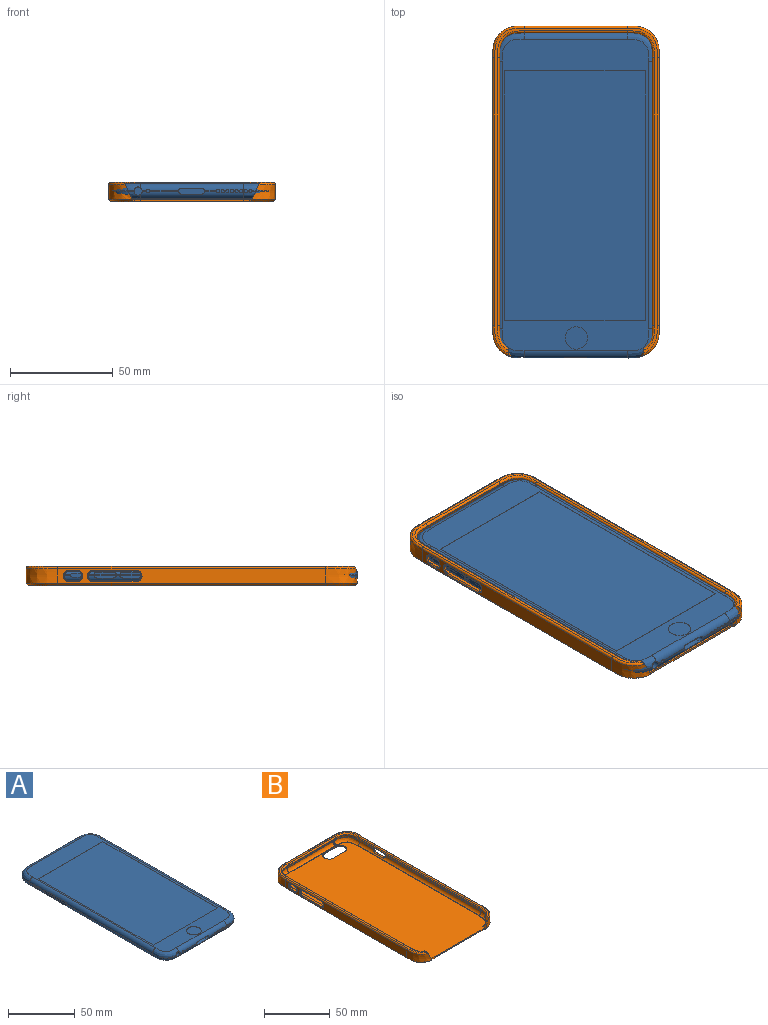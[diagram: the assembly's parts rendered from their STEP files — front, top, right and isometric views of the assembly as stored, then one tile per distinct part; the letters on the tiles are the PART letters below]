
ASSEMBLY  parts=2 mates=1
PART A: 108 faces, bbox 79.2x158.7x8 mm
  f0: plane 4.66x0.2mm, normal (-1,0,0), area 0.9mm2, adj f20,f43,f51,f102
  f1: plane 1.68x0.2mm, normal (-1,0,0), area 0.3mm2, adj f43,f51,f90,f95
  f2: plane 5.7x0.2mm, normal (-1,0,0), area 1.1mm2, adj f43,f51,f88,f104
  f3: plane 103.64x0.2mm, normal (1,0,0), area 20.7mm2, adj f12,f42,f50,f81
  f4: plane 0.66x0.2mm, normal (0,-1,0), area 0.1mm2, adj f46,f54,f72,f74
  f5: plane 0.2x0.15mm, normal (0,-1,0), area 0mm2, adj f16,f46,f54,f72
  f6: plane 5.71x0.2mm, normal (0,-1,0), area 1.1mm2, adj f46,f54,f59,f70
  f7: plane 0.66x0.2mm, normal (0,-1,0), area 0.1mm2, adj f46,f54,f65,f74
  f8: plane 0.66x0.2mm, normal (0,-1,0), area 0.1mm2, adj f46,f54,f63,f65
  f9: plane 0.66x0.2mm, normal (0,-1,0), area 0.1mm2, adj f46,f54,f61,f63
  f10: plane 0.66x0.2mm, normal (0,-1,0), area 0.1mm2, adj f46,f54,f59,f61
  f11: plane 14.01x0.2mm, normal (0,-1,0), area 2.8mm2, adj f46,f54,f57,f68
  f12: extruded ~13.98x9.78mm, area 3.8mm2, adj f3,f44,f52,f78
  f13: extruded ~0.66x0.2mm, area 0.1mm2, adj f44,f52,f76,f78
  f14: plane 151.62x71.34mm, normal (0,0,1), area 2367.4mm2, adj f30,f32,f33,f34,f35,f47,f48,f49
  f15: plane 2.09x0.2mm, normal (0,-1,0), area 0.4mm2, adj f46,f54,f55,f57
  f16: extruded ~0.52x0.2mm, area 0.1mm2, adj f5,f44,f52,f76
  f17: plane 15.88x0.2mm, normal (1,0,0), area 3.2mm2, adj f18,f42,f50,f83
  f18: extruded ~14.13x14.13mm, area 4.7mm2, adj f17,f19,f38,f40,f48
  f19: plane 50.18x0.2mm, normal (0,1,0), area 10mm2, adj f18,f20,f37,f39,f47
  f20: extruded ~14.13x14.13mm, area 4.7mm2, adj f0,f19,f41,f49
  f21: plane 90.97x0.2mm, normal (-1,0,0), area 18.2mm2, adj f22,f43,f51,f97
  f22: extruded ~14.08x11.12mm, area 4.1mm2, adj f21,f45,f53,f55
  f23: plane 151.62x71.34mm, normal (0,0,-1), area 10708mm2, adj f24,f26,f28,f39,f40,f41,f42,f43
  f24: cylinder r=3.83mm len=7.66mm, axis (0,0,1), area 16.1mm2, adj f23,f25,f37,f38
  f25: plane 7.66x7.66mm, normal (0,0,-1), area 46.1mm2, adj f24
  f26: cylinder r=0.8mm len=1.6mm, axis (0,0,-1), area 0.5mm2, adj f23,f27
  f27: plane 1.6x1.6mm, normal (0,0,-1), area 2mm2, adj f26
  f28: cylinder r=2.06mm len=4.11mm, axis (0,0,-1), area 1.3mm2, adj f23,f29
  f29: plane 4.11x4.11mm, normal (0,0,-1), area 13.3mm2, adj f28
  f30: cylinder r=5.45mm len=10.9mm, axis (0,0,1), area 3.4mm2, adj f14,f31
  f31: plane 10.9x10.9mm, normal (0,0,1), area 93.3mm2, adj f30
  f32: plane 68.36x0.1mm, normal (0,-1,0), area 6.8mm2, adj f14,f33,f35,f36
  f33: plane 121.54x0.1mm, normal (1,0,0), area 12.2mm2, adj f14,f32,f34,f36
  f34: plane 68.36x0.1mm, normal (0,1,0), area 6.8mm2, adj f14,f33,f35,f36
  f35: plane 121.54x0.1mm, normal (-1,0,0), area 12.2mm2, adj f14,f32,f34,f36
  f36: plane 121.54x68.36mm, normal (0,0,1), area 8308.5mm2, adj f32,f33,f34,f35
  f37: bspline ~3.66x3.64mm, area 4.8mm2, adj f19,f24,f38,f39
  f38: bspline ~3.61x3.6mm, area 5.3mm2, adj f18,f24,f37,f40
  f39: cylinder r=3.55mm len=49.3mm, axis (-1,0,0), area 274.9mm2, adj f19,f23,f37,f41
  f40: bspline ~16.8x14.8mm, area 114.8mm2, adj f18,f23,f38,f42
  f41: bspline ~16.8x16.8mm, area 120.2mm2, adj f20,f23,f39,f43
  f42: cylinder r=3.55mm len=130.46mm, axis (0,1,0), area 727.5mm2, adj f3,f17,f23,f40,f44,f80
  f43: cylinder r=3.55mm len=130.46mm, axis (0,-1,0), area 727.5mm2, adj f0,f1,f2,f21,f23,f41,f45,f87
  f44: bspline ~16.8x16.8mm, area 118.5mm2, adj f12,f13,f16,f23,f42,f46,f76,f78
  f45: bspline ~16.8x16.8mm, area 117.7mm2, adj f22,f23,f43,f46,f55
  f46: cylinder r=3.55mm len=50.18mm, axis (1,0,0), area 255.6mm2, adj f4,f5,f6,f7,f8,f9,f10,f11
  f47: cylinder r=3.55mm len=50.18mm, axis (1,0,0), area 279.8mm2, adj f14,f19,f48,f49
  f48: bspline ~16.8x16.8mm, area 120.2mm2, adj f14,f18,f47,f50
  f49: bspline ~16.8x14.8mm, area 120.2mm2, adj f14,f20,f47,f51
  f50: cylinder r=3.55mm len=130.46mm, axis (0,-1,0), area 727.5mm2, adj f3,f14,f17,f48,f52,f86
  f51: cylinder r=3.55mm len=130.46mm, axis (0,1,0), area 727.5mm2, adj f0,f1,f2,f14,f21,f49,f53,f93
  f52: bspline ~16.8x16.8mm, area 118.4mm2, adj f12,f13,f14,f16,f50,f54,f76,f78
  f53: bspline ~16.8x16.8mm, area 117.7mm2, adj f14,f22,f51,f54,f55
  f54: cylinder r=3.55mm len=50.18mm, axis (-1,0,0), area 255.6mm2, adj f4,f5,f6,f7,f8,f9,f10,f11
  f55: cylinder r=2.01mm len=4.02mm, axis (0,-1,0), area 34.2mm2, adj f15,f22,f45,f46,f53,f54,f56
  f56: plane 4.02x4.02mm, normal (0,-1,0), area 12.7mm2, adj f55
  f57: cylinder r=0.8mm len=3mm, axis (0,-1,0), area 14.9mm2, adj f11,f15,f46,f54,f58
  f58: plane 1.6x1.6mm, normal (0,-1,0), area 2mm2, adj f57
  f59: cylinder r=0.8mm len=3mm, axis (0,-1,0), area 14.9mm2, adj f6,f10,f46,f54,f60
  f60: plane 1.6x1.6mm, normal (0,-1,0), area 2mm2, adj f59
  f61: cylinder r=0.8mm len=3mm, axis (0,-1,0), area 14.9mm2, adj f9,f10,f46,f54,f62
  f62: plane 1.6x1.6mm, normal (0,-1,0), area 2mm2, adj f61
  f63: cylinder r=0.8mm len=3mm, axis (0,-1,0), area 14.9mm2, adj f8,f9,f46,f54,f64
  f64: plane 1.6x1.6mm, normal (0,-1,0), area 2mm2, adj f63
  f65: cylinder r=0.8mm len=3mm, axis (0,-1,0), area 14.9mm2, adj f7,f8,f46,f54,f66
  f66: plane 1.6x1.6mm, normal (0,-1,0), area 2mm2, adj f65
  f67: plane 9.84x2.72mm, normal (0,0,-1), area 26.8mm2, adj f54,f68,f70,f71
  f68: cylinder r=1.47mm len=3mm, axis (0,-1,0), area 13.3mm2, adj f11,f46,f54,f67,f69,f71
  f69: plane 9.84x2.72mm, normal (0,0,1), area 26.8mm2, adj f46,f68,f70,f71
  f70: cylinder r=1.47mm len=3mm, axis (0,-1,0), area 13.3mm2, adj f6,f46,f54,f67,f69,f71
  f71: plane 12.79x2.95mm, normal (0,-1,0), area 35.9mm2, adj f67,f68,f69,f70
  f72: cylinder r=0.8mm len=3mm, axis (0,-1,0), area 15.1mm2, adj f4,f5,f46,f54,f73
  f73: plane 1.6x1.6mm, normal (0,-1,0), area 2mm2, adj f72
  f74: cylinder r=0.8mm len=3mm, axis (0,-1,0), area 15.1mm2, adj f4,f7,f46,f54,f75
  f75: plane 1.6x1.6mm, normal (0,-1,0), area 2mm2, adj f74
  f76: cylinder r=0.8mm len=3mm, axis (0,-1,0), area 14.9mm2, adj f13,f16,f44,f52,f77
  f77: plane 1.6x1.6mm, normal (0,-1,0), area 2mm2, adj f76
  f78: cylinder r=0.8mm len=2.96mm, axis (0,-1,0), area 14.6mm2, adj f12,f13,f44,f52,f79
  f79: plane 1.6x1.6mm, normal (0,-1,0), area 2mm2, adj f78
  f80: plane 10.93x1.3mm, normal (-1,0,0), area 13.4mm2, adj f42,f81,f82,f83
  f81: cylinder r=1.4mm len=2.8mm, axis (-1,0,0), area 1.3mm2, adj f3,f80,f82,f84,f85,f86
  f82: plane 8.14x0.3mm, normal (0,0,-1), area 2.4mm2, adj f80,f81,f83,f85
  f83: cylinder r=1.4mm len=2.8mm, axis (-1,0,0), area 1.3mm2, adj f17,f80,f82,f84,f85,f86
  f84: plane 8.14x0.3mm, normal (0,0,1), area 2.4mm2, adj f81,f83,f85,f86
  f85: plane 10.94x2.8mm, normal (1,0,0), area 28.9mm2, adj f81,f82,f83,f84
  f86: plane 10.93x1.3mm, normal (-1,0,0), area 13.4mm2, adj f50,f81,f83,f84
  f87: plane 10.94x1.32mm, normal (1,0,0), area 13.6mm2, adj f43,f88,f89,f90
  f88: cylinder r=1.4mm len=2.8mm, axis (1,0,0), area 1.3mm2, adj f2,f87,f89,f91,f92,f93
  f89: plane 8.14x0.3mm, normal (0,0,-1), area 2.4mm2, adj f87,f88,f90,f92
  f90: cylinder r=1.4mm len=2.8mm, axis (1,0,0), area 1.3mm2, adj f1,f87,f89,f91,f92,f93
  f91: plane 8.14x0.3mm, normal (0,0,1), area 2.4mm2, adj f88,f90,f92,f93
  f92: plane 10.94x2.8mm, normal (-1,0,0), area 28.9mm2, adj f88,f89,f90,f91
  f93: plane 10.93x1.28mm, normal (1,0,0), area 13.2mm2, adj f51,f88,f90,f91
  f94: plane 10.94x1.32mm, normal (1,0,0), area 13.6mm2, adj f43,f95,f96,f97
  f95: cylinder r=1.4mm len=2.8mm, axis (1,0,0), area 1.3mm2, adj f1,f94,f96,f98,f99,f100
  f96: plane 8.14x0.3mm, normal (0,0,-1), area 2.4mm2, adj f94,f95,f97,f99
  f97: cylinder r=1.4mm len=2.8mm, axis (1,0,0), area 1.3mm2, adj f21,f94,f96,f98,f99,f100
  f98: plane 8.14x0.3mm, normal (0,0,1), area 2.4mm2, adj f95,f97,f99,f100
  f99: plane 10.94x2.8mm, normal (-1,0,0), area 28.9mm2, adj f95,f96,f97,f98
  f100: plane 10.93x1.28mm, normal (1,0,0), area 13.2mm2, adj f51,f95,f97,f98
  f101: plane 5.6x0.89mm, normal (1,0,0), area 4.6mm2, adj f43,f102,f103,f104
  f102: cylinder r=0.98mm len=1.97mm, axis (1,0,0), area 1.3mm2, adj f0,f101,f103,f105,f106,f107
  f103: plane 3.64x0.43mm, normal (0,0,-1), area 1.6mm2, adj f101,f102,f104,f106
  f104: cylinder r=0.98mm len=1.97mm, axis (1,0,0), area 1.3mm2, adj f2,f101,f103,f105,f106,f107
  f105: plane 3.64x0.43mm, normal (0,0,1), area 1.6mm2, adj f102,f104,f106,f107
  f106: plane 5.61x1.97mm, normal (-1,0,0), area 10.2mm2, adj f102,f103,f104,f105
  f107: plane 5.6x0.88mm, normal (1,0,0), area 4.5mm2, adj f51,f102,f104,f105
PART B: 108 faces, bbox 81.6x161.8x9.7 mm
  f0: extruded ~15.39x11.51mm, area 145.7mm2, adj f23,f66,f82,f89
  f1: plane 159.64x79.46mm, normal (0,0,-1), area 12304.5mm2, adj f26,f27,f28,f29,f68,f69,f70,f71
  f2: extruded ~12.01x8.14mm, area 5.8mm2, adj f6,f10,f30,f67
  f3: extruded ~11.19x4.91mm, area 4.6mm2, adj f7,f16,f67,f81
  f4: extruded ~15.39x11.51mm, area 145.7mm2, adj f17,f67,f85,f95
  f5: extruded ~13.79x8.49mm, area 3.6mm2, adj f6,f7,f39,f67
  f6: bspline ~16.7x10.56mm, area 69.8mm2, adj f2,f5,f50,f67
  f7: bspline ~16.52x9.41mm, area 62.5mm2, adj f3,f5,f53,f67
  f8: plane 50.22x0.4mm, normal (0,-1,0), area 17.9mm2, adj f9,f11,f30,f46,f47,f48
  f9: extruded ~12.13x12.13mm, area 7.3mm2, adj f8,f10,f30,f34,f47
  f10: plane 130.46x0.36mm, normal (-1,0,0), area 46.5mm2, adj f2,f9,f30,f50
  f11: extruded ~12.13x12.13mm, area 7.3mm2, adj f8,f13,f30,f49
  f12: extruded ~12.01x8.14mm, area 5.8mm2, adj f13,f30,f36,f66
  f13: plane 130.46x0.36mm, normal (1,0,0), area 46.5mm2, adj f11,f12,f30,f35
  f14: plane 50.18x0.36mm, normal (0,-1,0), area 17.9mm2, adj f15,f20,f51,f78
  f15: extruded ~12.13x12.13mm, area 7.3mm2, adj f14,f16,f31,f79
  f16: plane 130.46x0.36mm, normal (-1,0,0), area 46.5mm2, adj f3,f15,f53,f80
  f17: plane 130.46x7.3mm, normal (1,0,0), area 878.7mm2, adj f4,f18,f87,f94,f104,f105,f106,f107
  f18: extruded ~15.57x15.5mm, area 189mm2, adj f17,f24,f88,f93
  f19: plane 158.46x79.18mm, normal (0,0,1), area 530.1mm2, adj f66,f67,f75,f76,f77,f78,f79,f80
  f20: extruded ~12.13x12.13mm, area 7.3mm2, adj f14,f22,f52,f77
  f21: extruded ~11.19x4.91mm, area 4.6mm2, adj f22,f32,f66,f75
  f22: plane 130.46x0.36mm, normal (1,0,0), area 46.5mm2, adj f20,f21,f33,f76
  f23: plane 130.46x7.3mm, normal (-1,0,0), area 758.1mm2, adj f0,f25,f83,f90,f96,f97,f98,f99
  f24: plane 50.19x7.31mm, normal (0,1,0), area 366.3mm2, adj f18,f25,f86,f92
  f25: extruded ~15.57x15.5mm, area 189mm2, adj f23,f24,f84,f91
  f26: cylinder r=4.85mm len=9.71mm, axis (0,0,1), area 15.3mm2, adj f1,f27,f29,f30
  f27: plane 12.06x1mm, normal (0,1,0), area 12.1mm2, adj f1,f26,f28,f30
  f28: cylinder r=4.85mm len=9.71mm, axis (0,0,1), area 15.3mm2, adj f1,f27,f29,f30
  f29: plane 12.06x1mm, normal (0,-1,0), area 12.1mm2, adj f1,f26,f28,f30
  f30: plane 157.67x74.44mm, normal (0,0,1), area 11374mm2, adj f2,f8,f9,f10,f11,f12,f13,f26
  f31: bspline ~16.8x16.8mm, area 89.3mm2, adj f15,f41,f51,f53
  f32: bspline ~16.53x9.44mm, area 62.5mm2, adj f21,f33,f45,f66
  f33: cylinder r=3.55mm len=130.46mm, axis (0,1,0), area 445.8mm2, adj f22,f32,f37,f38,f44,f52,f54,f56
  f34: bspline ~16.8x14.8mm, area 85.5mm2, adj f9,f41,f47,f50
  f35: cylinder r=3.55mm len=130.46mm, axis (0,-1,0), area 444.5mm2, adj f13,f36,f37,f38,f44,f49,f55,f56
  f36: bspline ~16.69x10.51mm, area 69.8mm2, adj f12,f35,f45,f66
  f37: plane 3.24x0.2mm, normal (1,0,0), area 0.6mm2, adj f33,f35,f43,f60
  f38: plane 3.28x0.2mm, normal (1,0,0), area 0.7mm2, adj f33,f35,f56,f61
  f39: plane 102.64x0.2mm, normal (-1,0,0), area 20.5mm2, adj f5,f50,f53,f63
  f40: plane 14.88x0.2mm, normal (-1,0,0), area 3mm2, adj f41,f50,f53,f65
  f41: extruded ~14.13x14.13mm, area 4.7mm2, adj f31,f34,f40,f42,f47
  f42: plane 50.18x0.2mm, normal (0,-1,0), area 10mm2, adj f41,f43,f46,f48,f51
  f43: extruded ~14.13x14.13mm, area 4.7mm2, adj f37,f42,f49,f52
  f44: plane 89.96x0.2mm, normal (1,0,0), area 18mm2, adj f33,f35,f45,f57
  f45: extruded ~13.79x8.49mm, area 3.6mm2, adj f32,f36,f44,f66
  f46: bspline ~3.66x3.64mm, area 3.5mm2, adj f8,f42,f47,f48
  f47: bspline ~3.61x3.6mm, area 3.8mm2, adj f8,f9,f34,f41,f46
  f48: cylinder r=3.55mm len=49.3mm, axis (-1,0,0), area 195.8mm2, adj f8,f42,f46,f49
  f49: bspline ~16.8x16.8mm, area 89.3mm2, adj f11,f35,f43,f48
  f50: cylinder r=3.55mm len=130.46mm, axis (0,1,0), area 491.9mm2, adj f6,f10,f34,f39,f40,f62,f63,f65
  f51: cylinder r=3.55mm len=50.18mm, axis (1,0,0), area 199.3mm2, adj f14,f31,f42,f52
  f52: bspline ~16.8x14.8mm, area 89.3mm2, adj f20,f33,f43,f51
  f53: cylinder r=3.55mm len=130.46mm, axis (0,-1,0), area 491.9mm2, adj f7,f16,f31,f39,f40,f63,f64,f65
  f54: plane 20.75x1.7mm, normal (0,0,-1), area 35.2mm2, adj f33,f56,f57,f96
  f55: plane 20.75x1.73mm, normal (0,0,1), area 35.9mm2, adj f35,f56,f57,f99
  f56: cylinder r=2.4mm len=4.8mm, axis (-1,0,0), area 9.6mm2, adj f33,f35,f38,f54,f55,f97
  f57: cylinder r=2.4mm len=4.8mm, axis (-1,0,0), area 9.6mm2, adj f33,f35,f44,f54,f55,f98
  f58: plane 3.64x1.71mm, normal (0,0,-1), area 6.2mm2, adj f33,f60,f61,f100
  f59: plane 3.64x1.72mm, normal (0,0,1), area 6.3mm2, adj f35,f60,f61,f103
  f60: cylinder r=2.4mm len=4.8mm, axis (-1,0,0), area 9.6mm2, adj f33,f35,f37,f58,f59,f101
  f61: cylinder r=2.4mm len=4.8mm, axis (-1,0,0), area 9.6mm2, adj f33,f35,f38,f58,f59,f102
  f62: plane 8.14x1.71mm, normal (0,0,1), area 14mm2, adj f50,f63,f65,f105
  f63: cylinder r=2.4mm len=4.8mm, axis (1,0,0), area 9.6mm2, adj f39,f50,f53,f62,f64,f104
  f64: plane 8.14x1.71mm, normal (0,0,-1), area 14mm2, adj f53,f63,f65,f106
  f65: cylinder r=2.4mm len=4.8mm, axis (1,0,0), area 9.6mm2, adj f40,f50,f53,f62,f64,f107
  f66: plane 8.72x4.72mm, normal (0.91,0,0.42), area 20.6mm2, adj f0,f12,f19,f21,f30,f32,f36,f45
  f67: plane 8.72x4.72mm, normal (-0.91,0,0.42), area 20.6mm2, adj f2,f3,f4,f5,f6,f7,f19,f30
  f68: extruded ~2.94x1mm, area 2.9mm2, adj f1,f30,f69,f74
  f69: plane 50.18x1mm, normal (0,-1,0), area 50.2mm2, adj f1,f30,f68,f70
  f70: extruded ~2.94x1mm, area 2.9mm2, adj f1,f30,f69,f71
  f71: cylinder r=1mm len=1.05mm, axis (0,0,1), area 1.4mm2, adj f1,f30,f70,f72,f89
  f72: plane 0.31x0.31mm, normal (1,0,0), area 0mm2, adj f66,f71,f89
  f73: plane 0.31x0.31mm, normal (-1,0,0), area 0mm2, adj f67,f74,f95
  f74: cylinder r=1mm len=1.05mm, axis (0,0,1), area 1.4mm2, adj f1,f30,f68,f73,f95
  f75: bspline ~14.76x6.42mm, area 20.9mm2, adj f19,f21,f66,f76
  f76: cylinder r=1mm len=130.46mm, axis (0,-1,0), area 204.9mm2, adj f19,f22,f75,f77
  f77: bspline ~15.06x15.06mm, area 33mm2, adj f19,f20,f76,f78
  f78: cylinder r=1mm len=50.18mm, axis (-1,0,0), area 78.8mm2, adj f14,f19,f77,f79
  f79: bspline ~15.06x15.06mm, area 33mm2, adj f15,f19,f78,f80
  f80: cylinder r=1mm len=130.46mm, axis (0,1,0), area 204.9mm2, adj f16,f19,f79,f81
  f81: bspline ~14.76x6.42mm, area 20.9mm2, adj f3,f19,f67,f80
  f82: bspline ~16.91x9.15mm, area 27.3mm2, adj f0,f19,f66,f83
  f83: cylinder r=1mm len=130.46mm, axis (0,1,0), area 204.9mm2, adj f19,f23,f82,f84
  f84: bspline ~17.43x17.04mm, area 39.5mm2, adj f19,f25,f83,f86
  f85: bspline ~16.91x9.15mm, area 27.3mm2, adj f4,f19,f67,f87
  f86: cylinder r=1mm len=50.18mm, axis (1,0,0), area 78.8mm2, adj f19,f24,f84,f88
  f87: cylinder r=1mm len=130.46mm, axis (0,-1,0), area 204.9mm2, adj f17,f19,f85,f88
  f88: bspline ~17.43x17.04mm, area 39.5mm2, adj f18,f19,f86,f87
  f89: bspline ~15.46x12.81mm, area 29.8mm2, adj f0,f1,f71,f72,f90
  f90: plane 130.46x1mm, normal (-0.71,0,-0.71), area 184.5mm2, adj f1,f23,f89,f91
  f91: bspline ~15.5x15.5mm, area 35.3mm2, adj f1,f25,f90,f92
  f92: plane 50.18x1mm, normal (0,0.71,-0.71), area 71mm2, adj f1,f24,f91,f93
  f93: bspline ~15.5x15.5mm, area 35.3mm2, adj f1,f18,f92,f94
  f94: plane 130.46x1mm, normal (0.71,0,-0.71), area 184.5mm2, adj f1,f17,f93,f95
  f95: bspline ~15.46x12.81mm, area 29.8mm2, adj f1,f4,f73,f74,f94
  f96: plane 20.75x0.5mm, normal (-0.71,0,-0.71), area 14.7mm2, adj f23,f54,f97,f98
  f97: cone r=2.4mm half-angle=45deg, axis (-1,0,0), area 5.9mm2, adj f23,f56,f96,f99
  f98: cone r=2.4mm half-angle=45deg, axis (-1,0,0), area 5.9mm2, adj f23,f57,f96,f99
  f99: plane 20.75x0.5mm, normal (-0.71,0,0.71), area 14.7mm2, adj f23,f55,f97,f98
  f100: plane 3.64x0.5mm, normal (-0.71,0,-0.71), area 2.6mm2, adj f23,f58,f101,f102
  f101: cone r=2.4mm half-angle=45deg, axis (-1,0,0), area 5.9mm2, adj f23,f60,f100,f103
  f102: cone r=2.4mm half-angle=45deg, axis (-1,0,0), area 5.9mm2, adj f23,f61,f100,f103
  f103: plane 3.64x0.5mm, normal (-0.71,0,0.71), area 2.6mm2, adj f23,f59,f101,f102
  f104: cone r=2.4mm half-angle=45deg, axis (1,0,0), area 5.9mm2, adj f17,f63,f105,f106
  f105: plane 8.14x0.5mm, normal (0.71,0,0.71), area 5.8mm2, adj f17,f62,f104,f107
  f106: plane 8.14x0.5mm, normal (0.71,0,-0.71), area 5.8mm2, adj f17,f64,f104,f107
  f107: cone r=2.4mm half-angle=45deg, axis (1,0,0), area 5.9mm2, adj f17,f65,f105,f106
PLACE A t=(-4.92,6.69,-4.35)mm
PLACE B t=(-4.73,8.29,-4.8)mm fixed
MATE slider B.f30 <-> A.f23  axis (0,0,1) through (-5.05,6.27,-4.8)mm
